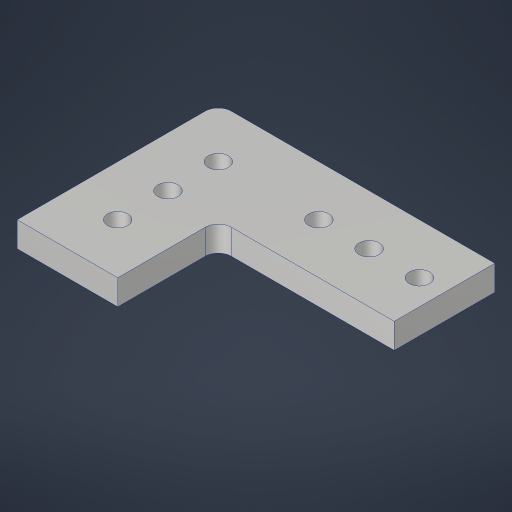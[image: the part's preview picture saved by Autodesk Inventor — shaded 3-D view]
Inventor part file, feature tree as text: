
AUTODESK INVENTOR PART (.ipt)
format: ipt  version: 2023.4 (Build 274418000, 418)  size: 246,784 bytes
history: native  units: in
note: dims shown in document units (in); Inventor stores cm internally (conversion verified against a paired STEP export)
features: sketch x3, extrude x2, hole x1, fillet x1
ambient origin geometry x8: Origin, YZ Plane, XZ Plane, XY Plane, X Axis, Y Axis, Z Axis, Center Point
bodies: Solid1 (feature_tree)
feature tree (7):
  extrude  "Extrusion1"  Depth=2.0in
  extrude  "Extrusion2"  Depth=1.0in
  hole  "Hole2"  [1 undecoded]
  fillet  "Fillet1"  Radius=0.5in
  sketch  "Sketch1"  dims[d0=1.0in d1=2.0in]
  sketch  "Sketch3"  dims[d2=0.25in d3=0.0in d14=1.0in]
  sketch  "Sketch4"  dims[d15=1.75in d16=0.0in d17=0.5in d18=0.5in d19=0.5in d20=1.0in d21=0.5in d22=0.5in d23=0.201in d24=0.75in d25=0.375in d26=0.25in d27=0.5635in d28=1.0in d29=0.8108in d30=0.13in]
note: 1 required parameter value undecoded (feature->parameter linkage not recoverable at this tier; creation-order binding heuristic only, values carry confidence <= 0.55)
